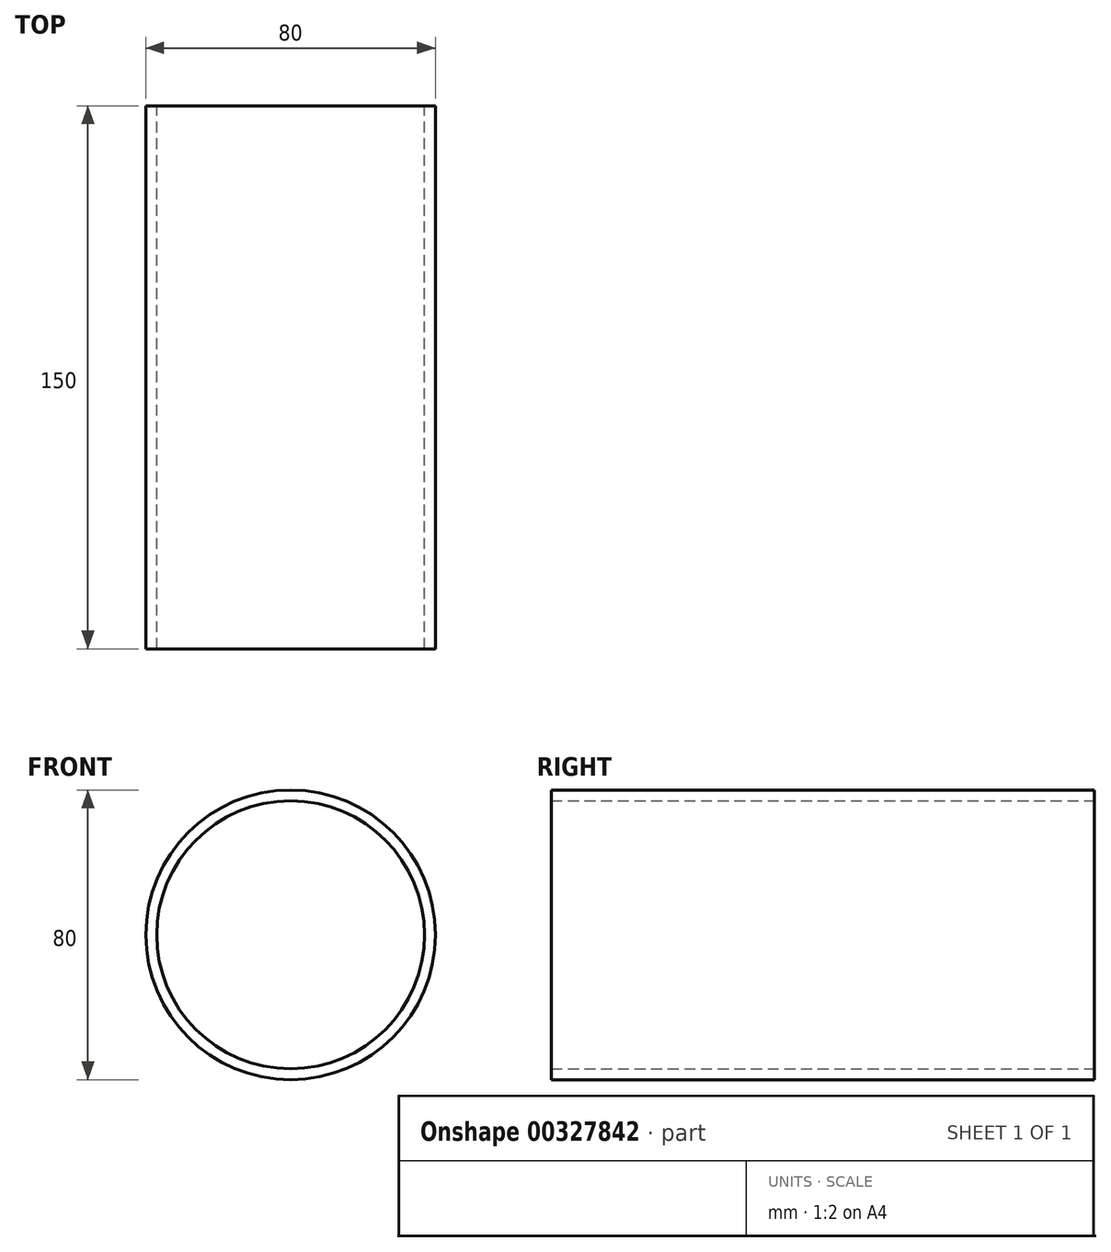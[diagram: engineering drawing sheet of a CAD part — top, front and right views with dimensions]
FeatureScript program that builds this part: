
annotation { "Feature Type Name" : "Feature", "Feature Type Description" : "" }
export const myFeature = defineFeature(function(context is Context, id is Id, definition is map)
    precondition{}
    {
        {
            var Q0;
            Q0=qCreatedBy(makeId("Front.planeOp"),FACE);
            var sketch = newSketch(context, id + "F0", { "sketchPlane" : qUnion([Q0])});
            skCircle(sketch, "E0", {"center": v(0, 0) * mm, "radius": 40 * mm});
            skCircle(sketch, "E1.0", {"center": v(0, 0) * mm, "radius": 37 * mm});
            skSolve(sketch);
        }
        {
            var Q0;
            Q0=qSketchRegion(id+"F0",true);
            extrude(context, id + "F1", {"entities" : qUnion([Q0]), "depth" : 150 * mm});
        }
    });
